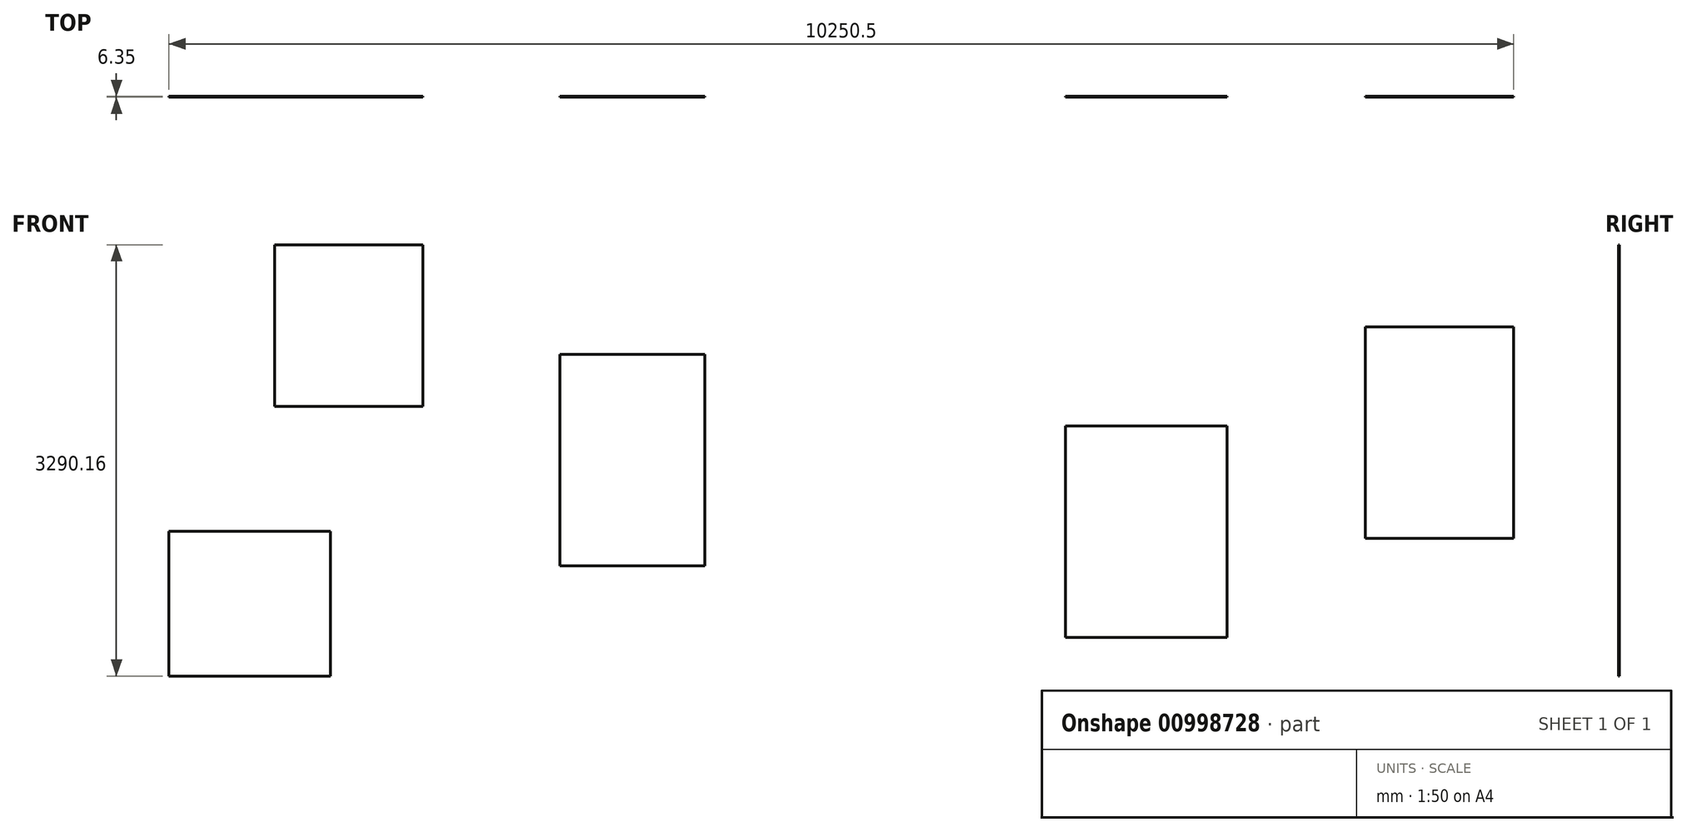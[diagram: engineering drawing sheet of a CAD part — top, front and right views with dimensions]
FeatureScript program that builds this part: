
annotation { "Feature Type Name" : "Feature", "Feature Type Description" : "" }
export const myFeature = defineFeature(function(context is Context, id is Id, definition is map)
    precondition{}
    {
        {
            var Q0;
            Q0=qCreatedBy(makeId("Front.planeOp"),FACE);
            var sketch = newSketch(context, id + "F0", { "sketchPlane" : qUnion([Q0])});
            skLineSegment(sketch, "E0.bottom", {"start": v(-599.7, 1905.95) * mm, "end": v(619.5, 1905.95) * mm});
            skLineSegment(sketch, "E0.top", {"start": v(-599.7, -532.45) * mm, "end": v(619.5, -532.45) * mm});
            skLineSegment(sketch, "E0.left", {"start": v(-599.7, 1905.95) * mm, "end": v(-599.7, -532.45) * mm});
            skLineSegment(sketch, "E0.right", {"start": v(619.5, 1905.95) * mm, "end": v(619.5, -532.45) * mm});
            skSolve(sketch);
        }
        {
            var Q0;
            Q0=makeQuery(id+"F0.imprint","IMPRINT",FACE,{"disambiguationData":[TD([[makeQuery(id+"F0.imprint","IMPRINT",EDGE,{"derivedFrom":sQuery(id+"F0.wireOp",EDGE,"E0.bottom")}),-1.0]])]});
            extrude(context, id + "F1", {"entities" : qUnion([Q0]), "depth" : 6.35 * mm, "offsetDistance" : 25.4 * mm});
        }
        {
            var Q0;
            Q0=qCreatedBy(makeId("Front.planeOp"),FACE);
            var sketch = newSketch(context, id + "F2", { "sketchPlane" : qUnion([Q0])});
            skLineSegment(sketch, "E1.bottom", {"start": v(-2647.56, 771.77) * mm, "end": v(-1542.66, 771.77) * mm});
            skLineSegment(sketch, "E1.top", {"start": v(-2647.56, -841.13) * mm, "end": v(-1542.66, -841.13) * mm});
            skLineSegment(sketch, "E1.left", {"start": v(-2647.56, 771.77) * mm, "end": v(-2647.56, -841.13) * mm});
            skLineSegment(sketch, "E1.right", {"start": v(-1542.66, 771.77) * mm, "end": v(-1542.66, -841.13) * mm});
            skSolve(sketch);
        }
        {
            var Q0;
            Q0=makeQuery(id+"F2.imprint","IMPRINT",FACE,{"disambiguationData":[TD([[makeQuery(id+"F2.imprint","IMPRINT",EDGE,{"derivedFrom":sQuery(id+"F2.wireOp",EDGE,"E1.bottom")}),-1.0]])]});
            extrude(context, id + "F3", {"entities" : qUnion([Q0]), "depth" : 6.35 * mm, "offsetDistance" : 25.4 * mm});
        }
        {
            var Q0;
            Q0=qCreatedBy(makeId("Front.planeOp"),FACE);
            var sketch = newSketch(context, id + "F4", { "sketchPlane" : qUnion([Q0])});
            skLineSegment(sketch, "E2.bottom", {"start": v(1207.99, 224.46) * mm, "end": v(2439.89, 224.46) * mm});
            skLineSegment(sketch, "E2.top", {"start": v(1207.99, -1388.44) * mm, "end": v(2439.89, -1388.44) * mm});
            skLineSegment(sketch, "E2.left", {"start": v(1207.99, 224.46) * mm, "end": v(1207.99, -1388.44) * mm});
            skLineSegment(sketch, "E2.right", {"start": v(2439.89, 224.46) * mm, "end": v(2439.89, -1388.44) * mm});
            skSolve(sketch);
        }
        {
            var Q0;
            Q0=makeQuery(id+"F4.imprint","IMPRINT",FACE,{"disambiguationData":[TD([[makeQuery(id+"F4.imprint","IMPRINT",EDGE,{"derivedFrom":sQuery(id+"F4.wireOp",EDGE,"E2.bottom")}),-1.0]])]});
            extrude(context, id + "F5", {"entities" : qUnion([Q0]), "depth" : 6.35 * mm, "offsetDistance" : 25.4 * mm});
        }
        {
            var Q0;
            Q0=qCreatedBy(makeId("Front.planeOp"),FACE);
            var sketch = newSketch(context, id + "F6", { "sketchPlane" : qUnion([Q0])});
            skLineSegment(sketch, "E3.bottom", {"start": v(-5627.75, -1682.25) * mm, "end": v(-5627.75, -577.35) * mm});
            skLineSegment(sketch, "E3.top", {"start": v(-4395.85, -1682.25) * mm, "end": v(-4395.85, -577.35) * mm});
            skLineSegment(sketch, "E3.left", {"start": v(-5627.75, -1682.25) * mm, "end": v(-4395.85, -1682.25) * mm});
            skLineSegment(sketch, "E3.right", {"start": v(-5627.75, -577.35) * mm, "end": v(-4395.85, -577.35) * mm});
            skSolve(sketch);
        }
        {
            var Q0;
            Q0=makeQuery(id+"F6.imprint","IMPRINT",FACE,{"disambiguationData":[TD([[makeQuery(id+"F6.imprint","IMPRINT",EDGE,{"derivedFrom":sQuery(id+"F6.wireOp",EDGE,"E3.bottom")}),-1.0]])]});
            extrude(context, id + "F7", {"entities" : qUnion([Q0]), "depth" : 6.35 * mm, "offsetDistance" : 25.4 * mm});
        }
        {
            var Q0;
            Q0=qCreatedBy(makeId("Front.planeOp"),FACE);
            var sketch = newSketch(context, id + "F8", { "sketchPlane" : qUnion([Q0])});
            skLineSegment(sketch, "E4.bottom", {"start": v(-4824.14, 1607.9) * mm, "end": v(-3693.84, 1607.9) * mm});
            skLineSegment(sketch, "E4.top", {"start": v(-4824.14, 376) * mm, "end": v(-3693.84, 376) * mm});
            skLineSegment(sketch, "E4.left", {"start": v(-4824.14, 1607.9) * mm, "end": v(-4824.14, 376) * mm});
            skLineSegment(sketch, "E4.right", {"start": v(-3693.84, 1607.9) * mm, "end": v(-3693.84, 376) * mm});
            skSolve(sketch);
        }
        {
            var Q0;
            Q0=makeQuery(id+"F8.imprint","IMPRINT",FACE,{"disambiguationData":[TD([[makeQuery(id+"F8.imprint","IMPRINT",EDGE,{"derivedFrom":sQuery(id+"F8.wireOp",EDGE,"E4.bottom")}),-1.0]])]});
            extrude(context, id + "F9", {"entities" : qUnion([Q0]), "depth" : 6.35 * mm, "offsetDistance" : 25.4 * mm});
        }
        {
            var Q0;
            Q0=qCreatedBy(makeId("Front.planeOp"),FACE);
            var sketch = newSketch(context, id + "F10", { "sketchPlane" : qUnion([Q0])});
            skLineSegment(sketch, "E5.bottom", {"start": v(3492.46, 981.86) * mm, "end": v(4622.76, 981.86) * mm});
            skLineSegment(sketch, "E5.top", {"start": v(3492.46, -631.04) * mm, "end": v(4622.76, -631.04) * mm});
            skLineSegment(sketch, "E5.left", {"start": v(3492.46, 981.86) * mm, "end": v(3492.46, -631.04) * mm});
            skLineSegment(sketch, "E5.right", {"start": v(4622.76, 981.86) * mm, "end": v(4622.76, -631.04) * mm});
            skSolve(sketch);
        }
        {
            var Q0;
            Q0=makeQuery(id+"F10.imprint","IMPRINT",FACE,{"disambiguationData":[TD([[makeQuery(id+"F10.imprint","IMPRINT",EDGE,{"derivedFrom":sQuery(id+"F10.wireOp",EDGE,"E5.bottom")}),-1.0]])]});
            extrude(context, id + "F11", {"entities" : qUnion([Q0]), "depth" : 6.35 * mm, "offsetDistance" : 25.4 * mm});
        }
        {
            var Q0;
            Q0=makeQuery(id+"F1.opExtrude","SWEPT_BODY",BODY,{"disambiguationData":[OSD([sQuery(id+"F0.wireOp",EDGE,"E0.bottom"),sQuery(id+"F0.wireOp",EDGE,"E0.top"),sQuery(id+"F0.wireOp",EDGE,"E0.left"),sQuery(id+"F0.wireOp",EDGE,"E0.right")])]});
            deleteBodies(context, id + "F12", {"entities" : qUnion([Q0])});
        }
    });
